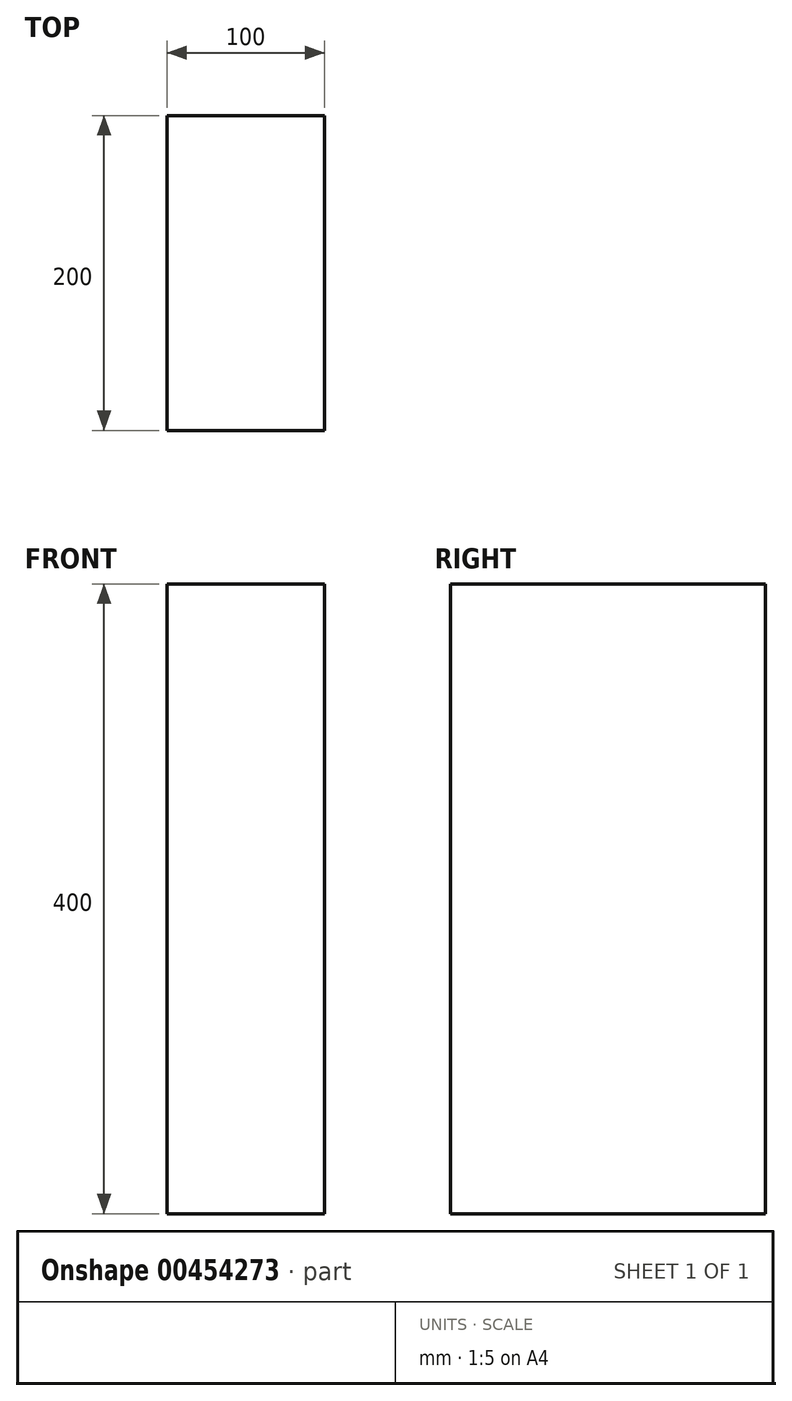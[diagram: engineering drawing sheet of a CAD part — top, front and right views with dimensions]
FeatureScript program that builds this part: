
annotation { "Feature Type Name" : "Feature", "Feature Type Description" : "" }
export const myFeature = defineFeature(function(context is Context, id is Id, definition is map)
    precondition{}
    {
        {
            var Q0;
            Q0=qCreatedBy(makeId("Front.planeOp"),FACE);
            var sketch = newSketch(context, id + "F0", { "sketchPlane" : qUnion([Q0])});
            skLineSegment(sketch, "E0.bottom", {"start": v(50, 200) * mm, "end": v(-50, 200) * mm});
            skLineSegment(sketch, "E0.top", {"start": v(50, -200) * mm, "end": v(-50, -200) * mm});
            skLineSegment(sketch, "E0.left", {"start": v(50, 200) * mm, "end": v(50, -200) * mm});
            skLineSegment(sketch, "E0.right", {"start": v(-50, 200) * mm, "end": v(-50, -200) * mm});
            skPoint(sketch, "E0.middle", {"position": v(0, 0) * mm});
            skSolve(sketch);
        }
        {
            var Q0;
            Q0 = qSketchRegion(id + "F0", true);
            extrude(context, id + "F1", {"entities" : qUnion([Q0]), "depth" : 200 * mm});
        }
    });
